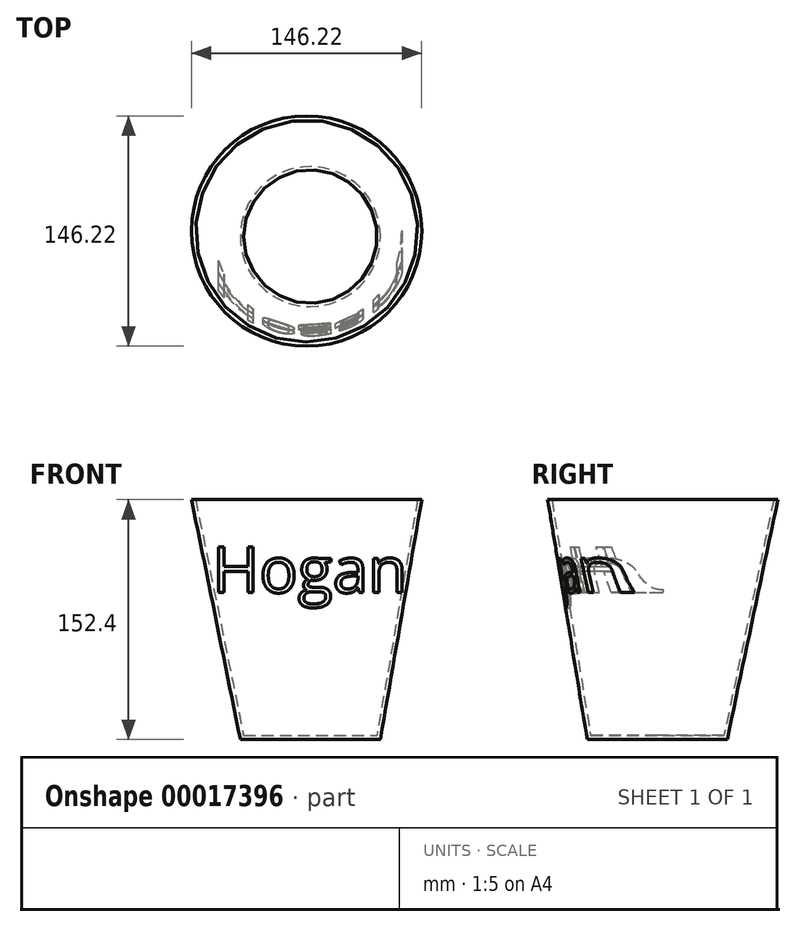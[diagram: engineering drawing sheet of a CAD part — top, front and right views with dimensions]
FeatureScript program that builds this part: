
annotation { "Feature Type Name" : "Feature", "Feature Type Description" : "" }
export const myFeature = defineFeature(function(context is Context, id is Id, definition is map)
    precondition{}
    {
        {
            var Q0;
            Q0=qCreatedBy(makeId("Top.planeOp"),FACE);
            var sketch = newSketch(context, id + "F0", { "sketchPlane" : qUnion([Q0])});
            skCircle(sketch, "E0", {"center": v(2.34, -3.55) * mm, "radius": 44.45 * mm});
            skSolve(sketch);
        }
        {
            var Q0;
            Q0=qCreatedBy(makeId("Top.planeOp"),FACE);
            cPlane(context, id + "F1", {"entities" : qUnion([Q0]), "cplaneType" : CPlaneType.OFFSET, "offset" : 152.4 * mm, "width" : 152.4 * mm, "height" : 152.4 * mm});
        }
        {
            var Q0;
            Q0=qCreatedBy(id+"F1.planeOp",FACE);
            var sketch = newSketch(context, id + "F2", { "sketchPlane" : qUnion([Q0])});
            skPoint(sketch, "E1.0", {"position": v(0, 0) * mm});
            skCircle(sketch, "E2", {"center": v(0, 0) * mm, "radius": 73.11 * mm});
            skSolve(sketch);
        }
        {
            var Q0;
            Q0=makeQuery(id+"F2.imprint","IMPRINT",FACE,{"disambiguationData":[TD([[makeQuery(id+"F2.imprint","IMPRINT",EDGE,{"derivedFrom":sQuery(id+"F2.wireOp",EDGE,"E2")}),1.0]])]});
            var Q1;
            Q1=makeQuery(id+"F0.imprint","IMPRINT",FACE,{"disambiguationData":[TD([[makeQuery(id+"F0.imprint","IMPRINT",EDGE,{"derivedFrom":sQuery(id+"F0.wireOp",EDGE,"E0")}),1.0]])]});
            loft(context, id + "F3", {"sheetProfilesArray" : [{ "sheetProfileEntities" : qUnion([Q0]) }, { "sheetProfileEntities" : qUnion([Q1]) }]});
        }
        {
            var Q0;
            Q0=makeQuery(id+"F3.opLoft","CAP_FACE",FACE,{"disambiguationData":[OSD([makeQuery(id+"F2.imprint","IMPRINT",FACE,{"disambiguationData":[TD([[makeQuery(id+"F2.imprint","IMPRINT",EDGE,{"derivedFrom":sQuery(id+"F2.wireOp",EDGE,"E2")}),1.0]])]})])],"isStart":true});
            shell(context, id + "F4", {"entities" : qUnion([Q0]), "thickness" : 2.54 * mm});
        }
        {
            var Q0;
            Q0=qCreatedBy(makeId("Front.planeOp"),FACE);
            var sketch = newSketch(context, id + "F5", { "sketchPlane" : qUnion([Q0])});
            skText(sketch, "E3", { "text": "Hogan", "fontName": "OpenSans-Regular.ttf"});
            const initialGuessF5  = {"E3": [-0.0599, 0.09333, 1, 0, 0.02913]};
            skSetInitialGuess(sketch, initialGuessF5);
            skSolve(sketch);
        }
        {
            var Q0;
            Q0 = qSketchRegion(id + "F5", true);
            extrude(context, id + "F6", {"entities" : qUnion([Q0]), "operationType" : NewBodyOperationType.INTERSECT, "depth" : 250.3 * mm});
        }
        {
            var Q0;
            Q0=makeQuery(id+"F0.imprint","IMPRINT",FACE,{"disambiguationData":[TD([[makeQuery(id+"F0.imprint","IMPRINT",EDGE,{"derivedFrom":sQuery(id+"F0.wireOp",EDGE,"E0")}),1.0]])]});
            var Q1;
            Q1=makeQuery(id+"F2.imprint","IMPRINT",FACE,{"disambiguationData":[TD([[makeQuery(id+"F2.imprint","IMPRINT",EDGE,{"derivedFrom":sQuery(id+"F2.wireOp",EDGE,"E2")}),1.0]])]});
            loft(context, id + "F7", {"sheetProfilesArray" : [{ "sheetProfileEntities" : qUnion([Q0]) }, { "sheetProfileEntities" : qUnion([Q1]) }]});
        }
        {
            var Q0;
            Q0=makeQuery(id+"F7.opLoft","CAP_FACE",FACE,{"disambiguationData":[OSD([makeQuery(id+"F2.imprint","IMPRINT",FACE,{"disambiguationData":[TD([[makeQuery(id+"F2.imprint","IMPRINT",EDGE,{"derivedFrom":sQuery(id+"F2.wireOp",EDGE,"E2")}),1.0]])]})])],"isStart":true});
            shell(context, id + "F8", {"entities" : qUnion([Q0]), "thickness" : 2.54 * mm});
        }
    });
